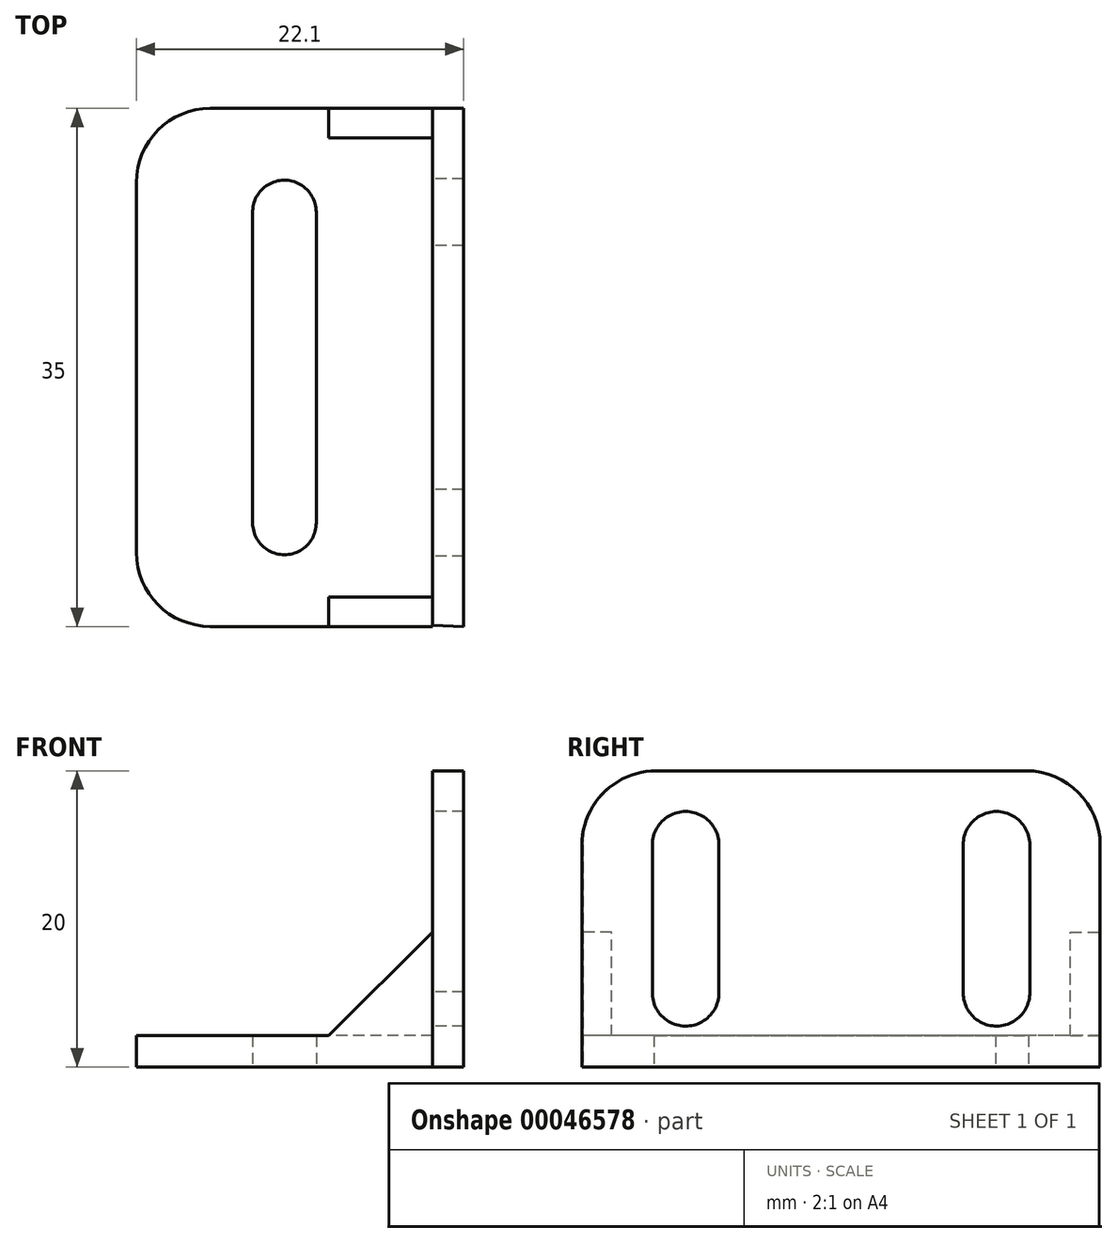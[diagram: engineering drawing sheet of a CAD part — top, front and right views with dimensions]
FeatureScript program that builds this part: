
annotation { "Feature Type Name" : "Feature", "Feature Type Description" : "" }
export const myFeature = defineFeature(function(context is Context, id is Id, definition is map)
    precondition{}
    {
        {
            var Q0;
            Q0=qCreatedBy(makeId("Top.planeOp"),FACE);
            var sketch = newSketch(context, id + "F0", { "sketchPlane" : qUnion([Q0])});
            skLineSegment(sketch, "E0", {"start": v(0, 0) * mm, "end": v(-15, 0) * mm});
            skLineSegment(sketch, "E1", {"start": v(-20, 5) * mm, "end": v(-20, 30) * mm});
            skLineSegment(sketch, "E2", {"start": v(-15, 35) * mm, "end": v(0, 35) * mm});
            skLineSegment(sketch, "E3", {"start": v(0, 35) * mm, "end": v(0, 0) * mm});
            skArc(sketch, "E4", {"start": v(-7.85, 28) * mm, "mid": v(-10.03, 30.15) * mm, "end": v(-12.15, 27.93) * mm});
            skArc(sketch, "E5", {"start": v(-12.15, 7) * mm, "mid": v(-10, 4.85) * mm, "end": v(-7.85, 7) * mm});
            skLineSegment(sketch, "E6", {"start": v(-12.15, 27.93) * mm, "end": v(-12.15, 7) * mm});
            skLineSegment(sketch, "E7", {"start": v(-7.85, 7) * mm, "end": v(-7.85, 28) * mm});
            skPoint(sketch, "E8.start.orphan", {"position": v(-10, 0) * mm});
            skPoint(sketch, "E9.orphan", {"position": v(-10, 35) * mm});
            skPoint(sketch, "E10.visualSharp", {"position": v(-20, 35) * mm});
            skArc(sketch, "E10.filletArc", {"start": v(-15, 35) * mm, "mid": v(-18.54, 33.54) * mm, "end": v(-20, 30) * mm});
            skPoint(sketch, "E11.visualSharp", {"position": v(-20, 0) * mm});
            skArc(sketch, "E11.filletArc", {"start": v(-20, 5) * mm, "mid": v(-18.54, 1.46) * mm, "end": v(-15, 0) * mm});
            skSolve(sketch);
        }
        {
            var Q0;
            Q0 = qSketchRegion(id + "F0", true);
            extrude(context, id + "F1", {"entities" : qUnion([Q0]), "depth" : 2.1 * mm});
        }
        {
            var Q0;
            Q0=qCreatedBy(makeId("Top.planeOp"),FACE);
            var sketch = newSketch(context, id + "F2", { "sketchPlane" : qUnion([Q0])});
            skLineSegment(sketch, "E12", {"start": v(0, 0) * mm, "end": v(0, 35) * mm});
            skLineSegment(sketch, "E13", {"start": v(0, 35) * mm, "end": v(2.1, 35) * mm});
            skLineSegment(sketch, "E14", {"start": v(2.1, 35) * mm, "end": v(2.1, 0) * mm});
            skLineSegment(sketch, "E15", {"start": v(2.1, 0) * mm, "end": v(-0.1, 0.08) * mm});
            skSolve(sketch);
        }
        {
            var Q0;
            Q0 = qSketchRegion(id + "F2", true);
            extrude(context, id + "F3", {"entities" : qUnion([Q0]), "operationType" : NewBodyOperationType.ADD, "depth" : 20 * mm});
        }
        {
            var Q0;
            Q0=qCreatedBy(makeId("Right.planeOp"),FACE);
            var sketch = newSketch(context, id + "F4", { "sketchPlane" : qUnion([Q0])});
            skArc(sketch, "E16", {"start": v(9.25, 15) * mm, "mid": v(7, 17.25) * mm, "end": v(4.75, 15) * mm});
            skLineSegment(sketch, "E17", {"start": v(0, 0) * mm, "end": v(7, 0) * mm});
            skArc(sketch, "E18", {"start": v(4.75, 5.06) * mm, "mid": v(6.97, 2.75) * mm, "end": v(9.25, 5) * mm});
            skLineSegment(sketch, "E19", {"start": v(4.75, 4.94) * mm, "end": v(4.75, 15) * mm});
            skLineSegment(sketch, "E20", {"start": v(9.25, 15) * mm, "end": v(9.25, 5) * mm});
            skLineSegment(sketch, "E21", {"start": v(0, 0) * mm, "end": v(35, 0) * mm});
            skLineSegment(sketch, "E22", {"start": v(17.5, 0) * mm, "end": v(17.5, -2.7) * mm});
            skLineSegment(sketch, "E23.MirrorCS", {"start": v(30.25, 4.94) * mm, "end": v(30.25, 15) * mm});
            skLineSegment(sketch, "E24.MirrorCS", {"start": v(25.75, 15) * mm, "end": v(25.75, 5) * mm});
            skArc(sketch, "E25.MirrorCS", {"start": v(30.25, 5.06) * mm, "mid": v(28.03, 2.75) * mm, "end": v(25.75, 5) * mm});
            skArc(sketch, "E26.MirrorCS", {"start": v(25.75, 15) * mm, "mid": v(28, 17.25) * mm, "end": v(30.25, 15) * mm});
            skSolve(sketch);
        }
        {
            var Q0;
            Q0 = qSketchRegion(id + "F4", true);
            extrude(context, id + "F5", {"entities" : qUnion([Q0]), "operationType" : NewBodyOperationType.REMOVE, "endBound" : BoundingType.UP_TO_NEXT, "depth" : 25 * mm});
        }
        {
            var Q0;
            Q0=makeQuery(id+"F3.opExtrude","CAP_EDGE",EDGE,{"disambiguationData":[OSD([sQuery(id+"F2.wireOp",EDGE,"E13")])],"isStart":false});
            var Q1;
            Q1=makeQuery(id+"F3.opExtrude","CAP_EDGE",EDGE,{"disambiguationData":[OSD([sQuery(id+"F2.wireOp",EDGE,"E15")])],"isStart":false});
            fillet(context, id + "F6", {"entities" : qUnion([Q0, Q1]), "radius" : 5 * mm, "tangentPropagation" : true, "allowEdgeOverflow" : false});
        }
        {
            var Q0;
            Q0=qCreatedBy(makeId("Front.planeOp"),FACE);
            var sketch = newSketch(context, id + "F7", { "sketchPlane" : qUnion([Q0])});
            skLineSegment(sketch, "E27", {"start": v(0, 0) * mm, "end": v(0, 2.1) * mm});
            skLineSegment(sketch, "E28", {"start": v(0, 2.1) * mm, "end": v(-7, 2.1) * mm});
            skLineSegment(sketch, "E29", {"start": v(0, 2.1) * mm, "end": v(0, 9.1) * mm});
            skLineSegment(sketch, "E30", {"start": v(0, 9.1) * mm, "end": v(-7, 2.1) * mm});
            skSolve(sketch);
        }
        {
            var Q0;
            Q0 = qSketchRegion(id + "F7", true);
            extrude(context, id + "F8", {"entities" : qUnion([Q0]), "operationType" : NewBodyOperationType.ADD, "oppositeDirection" : true, "depth" : 2 * mm});
        }
        {
            var Q0;
            Q0=makeQuery(id+"F3.boolean.opBoolean","MERGE",FACE,{"derivedFrom":[makeQuery(id+"F1.opExtrude","SWEPT_FACE",FACE,{"disambiguationData":[OSD([sQuery(id+"F0.wireOp",EDGE,"E2")])]}),makeQuery(id+"F3.opExtrude","SWEPT_FACE",FACE,{"disambiguationData":[OSD([sQuery(id+"F2.wireOp",EDGE,"E13")])]})]});
            cPlane(context, id + "F9", {"entities" : qUnion([Q0]), "cplaneType" : CPlaneType.OFFSET, "offset" : 0 * mm, "width" : 150 * mm, "height" : 150 * mm});
        }
        {
            var Q0;
            Q0=qCreatedBy(id+"F9.planeOp",FACE);
            var sketch = newSketch(context, id + "F10", { "sketchPlane" : qUnion([Q0])});
            skLineSegment(sketch, "E31", {"start": v(0, 0) * mm, "end": v(0, 2.1) * mm});
            skLineSegment(sketch, "E32", {"start": v(0, 2.1) * mm, "end": v(0, 9.1) * mm});
            skLineSegment(sketch, "E33", {"start": v(0, 2.1) * mm, "end": v(7, 2.1) * mm});
            skLineSegment(sketch, "E34", {"start": v(7, 2.1) * mm, "end": v(0, 9.1) * mm});
            skSolve(sketch);
        }
        {
            var Q0;
            Q0 = qSketchRegion(id + "F10", true);
            extrude(context, id + "F11", {"entities" : qUnion([Q0]), "operationType" : NewBodyOperationType.ADD, "oppositeDirection" : true, "depth" : 2 * mm});
        }
    });
